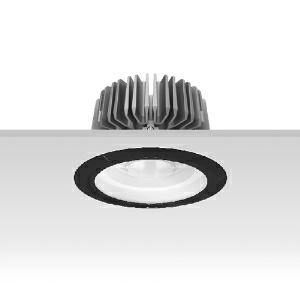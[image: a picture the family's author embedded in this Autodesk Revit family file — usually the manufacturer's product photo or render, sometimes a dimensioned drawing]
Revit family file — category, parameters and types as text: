
# Revit family: 3f_filippi_-_3f_reno_bianco_ampio_3f_filippi_-_30345_a01024_-_3f_reno_150_wh_2000-930_wide___vt_bk_0684
name_source: partatom
category: Lighting Fixtures
units: mm (PartAtom-declared; Revit-internal decimal feet)

## family parameters
Cut with Voids When Loaded = No
Host = Face
Light Source = No
Part Type = Normal
Room Calculation Point = No
Round Connector Dimension = Use Diameter
Shared = No

## types (1)
- 3F Filippi - 3F Reno Bianco Ampio (1 x LED, 1888 lm, 24 W, 3000 K)
    Apparent Load = 24 VA
    Approval mark = CE
    CIE Flux Codes = 74 93 99 100 100
    Color Rendering = 90
    Color Temperature = 3000 K
    Control Gear = Electronic ballast
    Default Elevation = 1800 mm
    Description = ILLUMINOTECHNICAL
Luminous efficiency 100% (DLOR 100%, ULOR 0%).
Initial luminous flux of the luminaire 1888 lm.
Direct symmetric wide distribution.
Installation Interdistance Transv.D = 1.54 x hu - Long.D = 1.54 x hu.
Tabular UGR (CIE 117 - 4H-8H; S=0.25H; 70/50/20): RUG 23.2 - 23.
Beam angle: 74° - 73°.
Luminous efficacy 79 lm/W.
Lifetime (L90/B10): 30000 h. (tq+25°C)
Lifetime (L85/B10): 50000 h. (tq+25°C)
Lifetime (L70/B10): 80000 h. (tq+25°C)
Sudden decreased luminous flux after 50000 hours: 0% (C0).
Photobiological safety in compliance with IEC/TR 62778: RG0 risk exempt, (IEC 62471).
In compliance with IEC/EN 62722-2-1 - IEC/EN 62717 standards.

SOURCE
Compact LED module 2000/930.
Energy efficiency class (UE 2019/2020 - UE 2019/2015): E.
CIE 13.3 Colour rendering index: CRI >90 (R9 >50%).
IES TM-30 Fidelity Index: Rf = 92 Rg = 101.
CCT nominal colour temperature 3000 K.
Colour initial tolerance (MacAdam): SDCM 3.
Zhaga Book 3 compliant.

MECHANICAL
Passive heat dissipator in die-casting aluminium, oversized, for optimum thermal management of the LED module.
Parabolic element with graduated/concentric rings in white polycarbonate.
Transparent external lens with glossy and satin differentiated surfaces, with a cooling and anti-insect system in methacrylate (PMMA).
Fastening spring clips in stainless steel.
Dimensions: diameter 176 mm, height 111 mm. Weight 0.81 kg.
IP44 protection degree for exposed part, IP20 for recessed part.
Mechanical strength to impacts IK06 (1 joule).
Glow-wire test resistance 650°C.

ELECTRICAL
Wiring on a separate unit.
Halogen Free electronic wiring 230V-50/60Hz, power factor 0.95, THD <25%, constant output current, SELV, class II, 1 driver.
Power of the luminaire 24 W.
ENEC - CE.
SAFE FLICKER: PstLM=<1 and SVM=<0.4 (IEC TR 61547-1 and IEC TR 63158), to ensure a more comfortable and safe light.
Luminaire compliant with EN 60598-2-22 for power supply from a centralised emergency system CPSS (Central Power Supply System), not incorporated in the luminaire - high risk areas excluded. The default power and flux are 100% in AC and 100% in DC.
Ambient temperature from 0°C to +25°C.
Temperature class T6 max 85°C.
Relative humidity UR: <85%.

INSTALLATION
Pull-up recessed fitting.
False ceiling carving: 150 mm.
All accessories dedicated to this product are available on the Catalog and on our website www.3F-Filippi.com.

ACCESSORIES
A01024 - VT transparent glass, tempered, not flammable, locked and in line with the trim, in black polycarbonate.

APPLICATIONS
Environments: architectural, commercial, exhibition areas, transit areas, corridors, shops, display windows, service areas.
In false ceilings with narrow voids.

WARNING
Luminaire designed for disposal/recycling at end-of-life.
Replaceable (LED only) light source by a professional. Replaceable control gear by a professional.
    Height = 0 mm  [stored 0 ft]
    Lamp = 1 x LED
    Lamp Light Flux = 1888 lm
    Lamp Power = 24 W
    Lamp count = 1
    Length = 176 mm
    Lifetime = 50000 h
    Luminous efficacy = 79 lm/W
    Manufacturer = 3F Filippi
    ModVariant = No
    Model = 3F Filippi - 30345+A01024 - 3F Reno 150 WH 2000-930 WIDE + VT BK
    Mounting Place = Ceiling
    Mounting Type = Recessed
    Number of Poles = 1
    OnlyDefault = Yes
    Power Factor = 1
    Product Name = 3F Filippi - 3F Reno Bianco Ampio
    Product group = recessed luminaire
    ProductGroupID = 4
    Protection Class = Protection class II
    Protection Degree = IP 20
    RLX_Detail_Level = 1
    RLX_Emergency_Light_Flux = 0 lm
    RLX_Emergency_Type = 0
    RLX_Emergency_Type_DB = No
    RlxData = <blob elided: 88637 chars, md5=8262b926>
    Socket = socket
    Standby Power = 0 W
    System Light Flux = 1888 lm
    System Power = 24 W
    Type Comments = Product without accessories
    Type Image = 3ffilippi_3f_reno_150_wh_d150__a01024.jpg
    URL = http://relux.com
    VarID = ---
    Voltage = 0 V
    Weight = 0.00 kg
    Width = 0 mm  [stored 0 ft]

note: [stored X ft] marks values corroborated as IEEE doubles in the binary element streams (Revit-internal decimal feet)

## geometry (parser evidence)
native form markers: Blend x4, Sweep x10
no freeform markers — native parametric forms only
